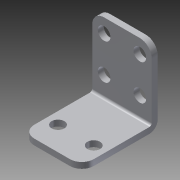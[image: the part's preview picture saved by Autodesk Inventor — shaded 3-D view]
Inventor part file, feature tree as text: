
AUTODESK INVENTOR PART (.ipt)
format: ipt  version: 2014 SP1 (Build 180222100, 222)  size: 214,528 bytes
history: native  units: in
note: dims shown in document units (in); Inventor stores cm internally (conversion verified against a paired STEP export)
features: other x3, sketch x2, sheet_metal_op x2, chamfer x1
ambient origin geometry x8: Origin, YZ Plane, XZ Plane, XY Plane, X Axis, Y Axis, Z Axis, Center Point
bodies: Solid1 (feature_tree)
feature tree (8):
  sketch  "Sketch1"  dims[d0=1.25in]
  sheet_metal_op  "Face1"
  sheet_metal_op  "Fold1"
  chamfer  "Corner Round1"
  other  "Plate1"
  sketch  "Sketch2"  dims[d3=0.266in d4=0.266in d7=1.5in d8=1.5in d9=0.125in d10=0.125in d11=0.0625in d12=0.25in d13=0.125in d14=90.0deg d15=0.05in d22=0.75in d26=0.5in d28=0.266in d29=1.0in d30=0.25in d31=0.7874in d33=0.75in d34=0.7874in d36=0.75in d39=0.25in d40=0.7874in d42=0.75in d43=0.7874in d45=0.75in d48=0.266in d49=0.55in d50=0.125in d51=0.0in d52=0.5in d53=0.1in d54=0.375in d55=1.25in]
  other  "Cut1"
  other  "Definition1"
